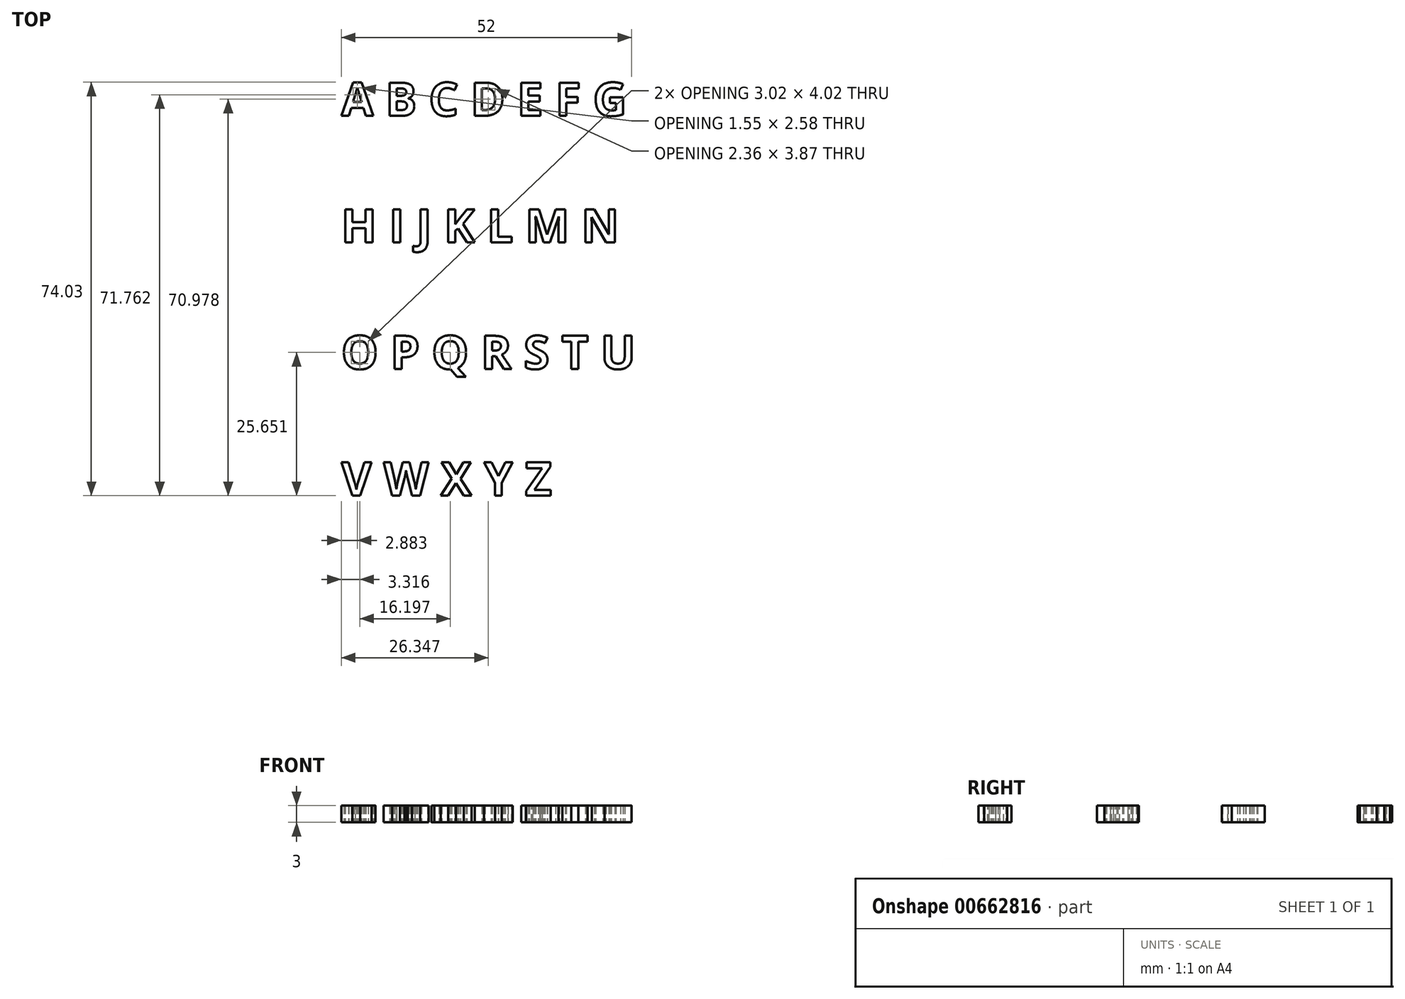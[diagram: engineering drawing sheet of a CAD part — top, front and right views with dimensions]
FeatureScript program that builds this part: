
annotation { "Feature Type Name" : "Feature", "Feature Type Description" : "" }
export const myFeature = defineFeature(function(context is Context, id is Id, definition is map)
    precondition{}
    {
        {
            var Q0;
            Q0=qCreatedBy(makeId("Top.planeOp"),FACE);
            var sketch = newSketch(context, id + "F0", { "sketchPlane" : qUnion([Q0])});
            skPoint(sketch, "E0.middle", {"position": v(-24.74, 7.18) * mm});
            skText(sketch, "E1", { "text": "A B C D E F G \n\nH I J K L M N\n\nO P Q R S T U\n\nV W X Y Z ", "fontName": "OpenSans-Bold.ttf"});
            const initialGuessF0  = {"E1": [-0.06653, 0.0315, 1, 0, 0.006]};
            skSetInitialGuess(sketch, initialGuessF0);
            skSolve(sketch);
        }
        {
            var Q0;
            Q0=qSketchRegion(id+"F0",true);
            extrude(context, id + "F1", {"entities" : qUnion([Q0]), "depth" : 3 * mm, "offsetDistance" : 25 * mm});
        }
    });
